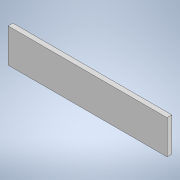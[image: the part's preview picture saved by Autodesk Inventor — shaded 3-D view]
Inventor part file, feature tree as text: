
AUTODESK INVENTOR PART (.ipt)
format: ipt  version: 2020.1 (Build 241239000, 239)  size: 93,184 bytes
history: native  units: in
note: dims shown in document units (in); Inventor stores cm internally (conversion verified against a paired STEP export)
features: extrude x1, sketch x1
ambient origin geometry x8: Origin, YZ Plane, XZ Plane, XY Plane, X Axis, Y Axis, Z Axis, Center Point
bodies: Solid1 (feature_tree)
feature tree (2):
  extrude  "Extrusion1"  Depth=84.0in
  sketch  "Sketch1"  dims[d0=196.0in d1=84.0in d2=197.0in d3=84.0in d4=12.0in d5=0.0in]
